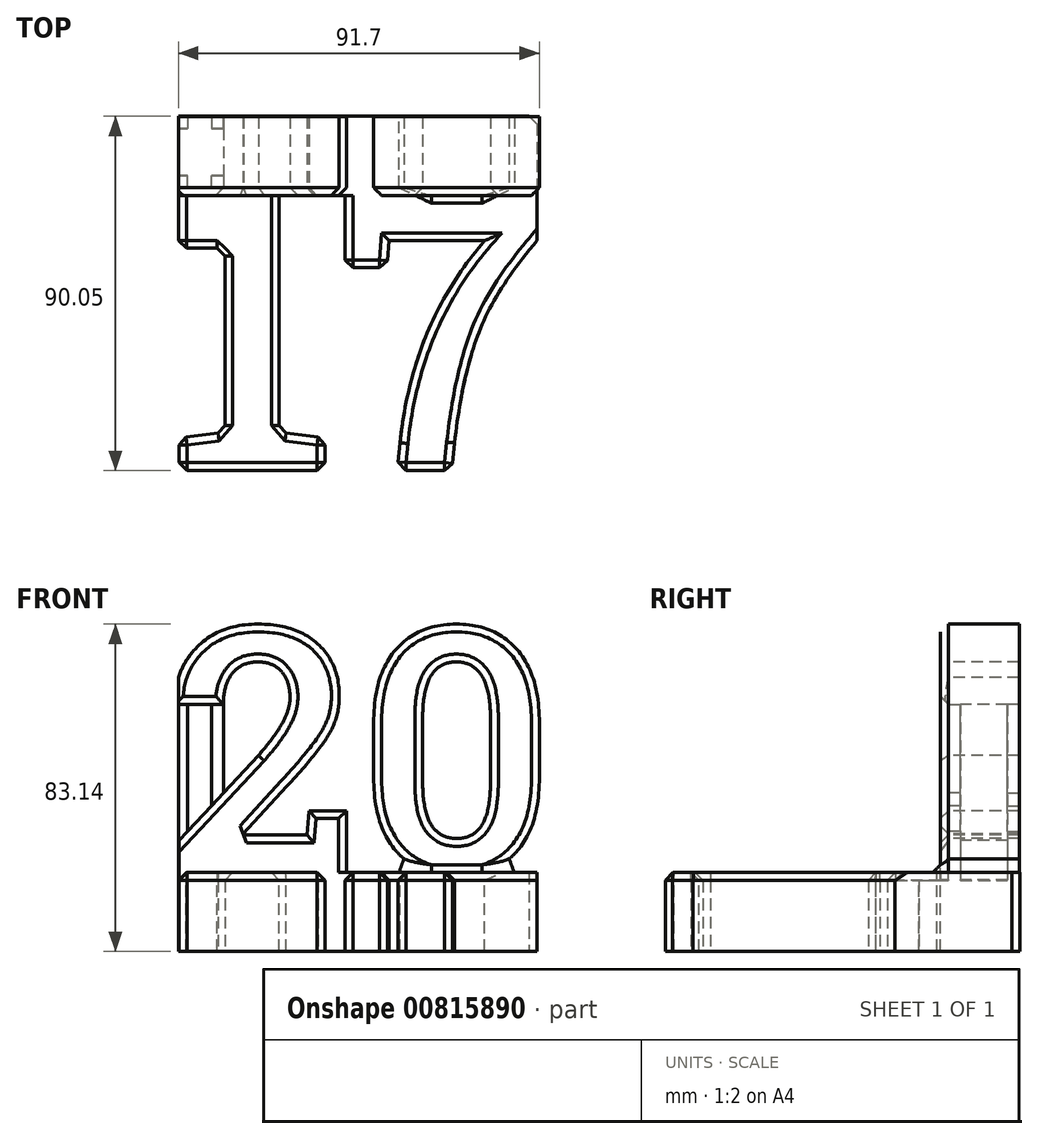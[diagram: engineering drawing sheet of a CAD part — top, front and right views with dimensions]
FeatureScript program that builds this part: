
annotation { "Feature Type Name" : "Feature", "Feature Type Description" : "" }
export const myFeature = defineFeature(function(context is Context, id is Id, definition is map)
    precondition{}
    {
        {
            var Q0;
            Q0=qCreatedBy(makeId("Top.planeOp"),FACE);
            var sketch = newSketch(context, id + "F0", { "sketchPlane" : qUnion([Q0])});
            skText(sketch, "E0", { "text": "17", "fontName": "RobotoSlab-Bold.ttf"});
            const initialGuessF0  = {"E0": [0, -0.06993, 1, 0, 0.06993]};
            skSetInitialGuess(sketch, initialGuessF0);
            skSolve(sketch);
        }
        {
            var Q0;
            Q0=makeQuery(id+"F0.imprint","IMPRINT",FACE,{"disambiguationData":[TD([[makeQuery(id+"F0.imprint","IMPRINT",EDGE,{"derivedFrom":sQuery(id+"F0.wireOp",EDGE,"E0.sketch_text.stroke-0")}),-1.0]])]});
            var Q1;
            Q1=makeQuery(id+"F0.imprint","IMPRINT",FACE,{"disambiguationData":[TD([[makeQuery(id+"F0.imprint","IMPRINT",EDGE,{"derivedFrom":sQuery(id+"F0.wireOp",EDGE,"E0.sketch_text.stroke-10")}),-1.0]])]});
            extrude(context, id + "F1", {"entities" : qUnion([Q0, Q1]), "oppositeDirection" : true, "depth" : 20 * mm, "offsetDistance" : 25 * mm});
        }
        {
            var Q0;
            Q0=qCreatedBy(makeId("Front.planeOp"),FACE);
            var sketch = newSketch(context, id + "F2", { "sketchPlane" : qUnion([Q0])});
            skText(sketch, "E1", { "text": "20", "fontName": "RobotoSlab-Bold.ttf"});
            const initialGuessF2  = {"E1": [0, 0, 1, 0, 0.06303]};
            skSetInitialGuess(sketch, initialGuessF2);
            skSolve(sketch);
        }
        {
            var Q0;
            Q0 = qSketchRegion(id + "F2", true);
            extrude(context, id + "F3", {"entities" : qUnion([Q0]), "oppositeDirection" : true, "depth" : 20 * mm, "offsetDistance" : 25 * mm});
        }
        {
            var Q0;
            Q0=makeQuery(id+"F1.opExtrude","SWEPT_FACE",FACE,{"disambiguationData":[OSD([sQuery(id+"F0.wireOp",EDGE,"E0.sketch_text.stroke-21")])]});
            var sketch = newSketch(context, id + "F4", { "sketchPlane" : qUnion([Q0])});
            skLineSegment(sketch, "E2.bottom", {"start": v(-94.05, -20) * mm, "end": v(0, -20) * mm});
            skLineSegment(sketch, "E2.top", {"start": v(-94.05, 0) * mm, "end": v(0, 0) * mm});
            skLineSegment(sketch, "E2.left", {"start": v(-94.05, -20) * mm, "end": v(-94.05, 0) * mm});
            skLineSegment(sketch, "E2.right", {"start": v(0, -20) * mm, "end": v(0, 0) * mm});
            skSolve(sketch);
        }
        {
            var Q0;
            Q0 = qSketchRegion(id + "F4", true);
            extrude(context, id + "F5", {"entities" : qUnion([Q0]), "operationType" : NewBodyOperationType.ADD, "depth" : 21 * mm, "offsetDistance" : 25 * mm});
        }
        {
            var Q0;
            Q0=makeQuery(id+"F5.opExtrude","CAP_FACE",FACE,{"disambiguationData":[OSD([sQuery(id+"F4.wireOp",EDGE,"E2.bottom"),sQuery(id+"F4.wireOp",EDGE,"E2.top"),sQuery(id+"F4.wireOp",EDGE,"E2.left"),sQuery(id+"F4.wireOp",EDGE,"E2.right")])],"isStart":true});
            var sketch = newSketch(context, id + "F6", { "sketchPlane" : qUnion([Q0])});
            skLineSegment(sketch, "E3.bottom", {"start": v(3, -20) * mm, "end": v(30, -20) * mm});
            skLineSegment(sketch, "E3.top", {"start": v(3, 0) * mm, "end": v(30, 0) * mm});
            skLineSegment(sketch, "E3.left", {"start": v(3, -20) * mm, "end": v(3, 0) * mm});
            skLineSegment(sketch, "E3.right", {"start": v(30, -20) * mm, "end": v(30, 0) * mm});
            skSolve(sketch);
        }
        {
            var Q0;
            Q0 = qSketchRegion(id + "F6", true);
            extrude(context, id + "F7", {"entities" : qUnion([Q0]), "operationType" : NewBodyOperationType.ADD, "depth" : 7 * mm, "offsetDistance" : 25 * mm});
        }
        {
            var Q0;
            Q0=makeQuery(id+"F7.opExtrude","CAP_FACE",FACE,{"disambiguationData":[OSD([sQuery(id+"F6.wireOp",EDGE,"E3.bottom"),sQuery(id+"F6.wireOp",EDGE,"E3.top"),sQuery(id+"F6.wireOp",EDGE,"E3.left"),sQuery(id+"F6.wireOp",EDGE,"E3.right")])],"isStart":false});
            extrude(context, id + "F8", {"entities" : qUnion([Q0]), "operationType" : NewBodyOperationType.REMOVE, "oppositeDirection" : true, "depth" : 7 * mm, "offsetDistance" : 25 * mm});
        }
        {
            var Q0;
            Q0=makeQuery(id+"F7.boolean.opBoolean","MERGE",FACE,{"derivedFrom":[makeQuery(id+"F1.opExtrude","CAP_FACE",FACE,{"disambiguationData":[OSD([sQuery(id+"F0.wireOp",EDGE,"E0.sketch_text.stroke-0"),sQuery(id+"F0.wireOp",EDGE,"E0.sketch_text.stroke-1"),sQuery(id+"F0.wireOp",EDGE,"E0.sketch_text.stroke-2"),sQuery(id+"F0.wireOp",EDGE,"E0.sketch_text.stroke-3"),sQuery(id+"F0.wireOp",EDGE,"E0.sketch_text.stroke-4"),sQuery(id+"F0.wireOp",EDGE,"E0.sketch_text.stroke-5"),sQuery(id+"F0.wireOp",EDGE,"E0.sketch_text.stroke-6"),sQuery(id+"F0.wireOp",EDGE,"E0.sketch_text.stroke-7"),sQuery(id+"F0.wireOp",EDGE,"E0.sketch_text.stroke-8"),sQuery(id+"F0.wireOp",EDGE,"E0.sketch_text.stroke-9")])],"isStart":true}),makeQuery(id+"F5.boolean.opBoolean","MERGE",FACE,{"derivedFrom":[makeQuery(id+"F1.opExtrude","CAP_FACE",FACE,{"disambiguationData":[OSD([sQuery(id+"F0.wireOp",EDGE,"E0.sketch_text.stroke-10"),sQuery(id+"F0.wireOp",EDGE,"E0.sketch_text.stroke-11"),sQuery(id+"F0.wireOp",EDGE,"E0.sketch_text.stroke-12"),sQuery(id+"F0.wireOp",EDGE,"E0.sketch_text.stroke-13"),sQuery(id+"F0.wireOp",EDGE,"E0.sketch_text.stroke-14"),sQuery(id+"F0.wireOp",EDGE,"E0.sketch_text.stroke-15"),sQuery(id+"F0.wireOp",EDGE,"E0.sketch_text.stroke-16"),sQuery(id+"F0.wireOp",EDGE,"E0.sketch_text.stroke-17"),sQuery(id+"F0.wireOp",EDGE,"E0.sketch_text.stroke-18"),sQuery(id+"F0.wireOp",EDGE,"E0.sketch_text.stroke-19"),sQuery(id+"F0.wireOp",EDGE,"E0.sketch_text.stroke-20"),sQuery(id+"F0.wireOp",EDGE,"E0.sketch_text.stroke-21"),sQuery(id+"F0.wireOp",EDGE,"E0.sketch_text.stroke-22")])],"isStart":true}),makeQuery(id+"F5.opExtrude","SWEPT_FACE",FACE,{"disambiguationData":[OSD([sQuery(id+"F4.wireOp",EDGE,"E2.top")])]})]}),makeQuery(id+"F7.opExtrude","SWEPT_FACE",FACE,{"disambiguationData":[OSD([sQuery(id+"F6.wireOp",EDGE,"E3.top")])]})]});
            var sketch = newSketch(context, id + "F9", { "sketchPlane" : qUnion([Q0])});
            skLineSegment(sketch, "E4.bottom", {"start": v(0, 20.12) * mm, "end": v(3, 20.12) * mm});
            skLineSegment(sketch, "E4.top", {"start": v(0, -0.88) * mm, "end": v(3, -0.88) * mm});
            skLineSegment(sketch, "E4.left", {"start": v(0, 20.12) * mm, "end": v(0, -0.88) * mm});
            skLineSegment(sketch, "E4.right", {"start": v(3, 20.12) * mm, "end": v(3, -0.88) * mm});
            skSolve(sketch);
        }
        {
            var Q0;
            Q0 = qSketchRegion(id + "F9", true);
            extrude(context, id + "F10", {"entities" : qUnion([Q0]), "operationType" : NewBodyOperationType.REMOVE, "oppositeDirection" : true, "depth" : 25 * mm, "offsetDistance" : 25 * mm});
        }
        {
            var Q0;
            Q0=makeQuery(id+"F5.boolean.opBoolean","MERGE",EDGE,{"derivedFrom":[makeQuery(id+"F1.opExtrude","CAP_EDGE",EDGE,{"disambiguationData":[OSD([sQuery(id+"F0.wireOp",EDGE,"E0.sketch_text.stroke-22")])],"isStart":true}),makeQuery(id+"F5.opExtrude","SWEPT_EDGE",EDGE,{"disambiguationData":[OSD([sQuery(id+"F4.wireOp",EDGE,"E2.top"),sQuery(id+"F4.wireOp",EDGE,"E2.left")])]})]});
            var Q1;
            Q1=makeQuery(id+"F1.opExtrude","CAP_EDGE",EDGE,{"disambiguationData":[OSD([sQuery(id+"F0.wireOp",EDGE,"E0.sketch_text.stroke-13")])],"isStart":true});
            var Q2;
            Q2=makeQuery(id+"F1.opExtrude","CAP_EDGE",EDGE,{"disambiguationData":[OSD([sQuery(id+"F0.wireOp",EDGE,"E0.sketch_text.stroke-14")])],"isStart":true});
            var Q3;
            Q3=makeQuery(id+"F1.opExtrude","CAP_EDGE",EDGE,{"disambiguationData":[OSD([sQuery(id+"F0.wireOp",EDGE,"E0.sketch_text.stroke-15")])],"isStart":true});
            var Q4;
            Q4=makeQuery(id+"F1.opExtrude","CAP_EDGE",EDGE,{"disambiguationData":[OSD([sQuery(id+"F0.wireOp",EDGE,"E0.sketch_text.stroke-16")])],"isStart":true});
            var Q5;
            Q5=makeQuery(id+"F1.opExtrude","CAP_EDGE",EDGE,{"disambiguationData":[OSD([sQuery(id+"F0.wireOp",EDGE,"E0.sketch_text.stroke-17")])],"isStart":true});
            var Q6;
            Q6=makeQuery(id+"F1.opExtrude","CAP_EDGE",EDGE,{"disambiguationData":[OSD([sQuery(id+"F0.wireOp",EDGE,"E0.sketch_text.stroke-18")])],"isStart":true});
            var Q7;
            Q7=makeQuery(id+"F1.opExtrude","CAP_EDGE",EDGE,{"disambiguationData":[OSD([sQuery(id+"F0.wireOp",EDGE,"E0.sketch_text.stroke-19")])],"isStart":true});
            var Q8;
            Q8=makeQuery(id+"F1.opExtrude","CAP_EDGE",EDGE,{"disambiguationData":[OSD([sQuery(id+"F0.wireOp",EDGE,"E0.sketch_text.stroke-20")])],"isStart":true});
            var Q9;
            Q9=makeQuery(id+"F1.opExtrude","CAP_EDGE",EDGE,{"disambiguationData":[OSD([sQuery(id+"F0.wireOp",EDGE,"E0.sketch_text.stroke-10")])],"isStart":true});
            var Q10;
            Q10=makeQuery(id+"F1.opExtrude","CAP_EDGE",EDGE,{"disambiguationData":[OSD([sQuery(id+"F0.wireOp",EDGE,"E0.sketch_text.stroke-11")])],"isStart":true});
            var Q11;
            Q11=makeQuery(id+"F1.opExtrude","CAP_EDGE",EDGE,{"disambiguationData":[OSD([sQuery(id+"F0.wireOp",EDGE,"E0.sketch_text.stroke-12")])],"isStart":true});
            var Q12;
            {var subQ0=sQuery(id+"F6.wireOp",EDGE,"E3.right");var subQ1=sQuery(id+"F6.wireOp",EDGE,"E3.left");var subQ2=sQuery(id+"F6.wireOp",EDGE,"E3.top");var subQ3=sQuery(id+"F6.wireOp",EDGE,"E3.bottom");var subQ4=sQuery(id+"F0.wireOp",EDGE,"E0.sketch_text.stroke-5");Q12=makeQuery(id+"F8.boolean.opBoolean","MERGE",EDGE,{"derivedFrom":[makeQuery(id+"F1.opExtrude","CAP_EDGE",EDGE,{"disambiguationData":[OSD([subQ4])],"isStart":true}),makeQuery(id+"F8.opExtrude","SWEPT_EDGE",EDGE,{"disambiguationData":[OSD([subQ4,subQ3,subQ2,subQ1,subQ0]),TDD([makeQuery(id+"F7.boolean.opBoolean","INTERSECT",VERTEX,{"disambiguationData":[OD(0.0)],"derivedFrom":[makeQuery(id+"F1.opExtrude","SWEPT_FACE",FACE,{"disambiguationData":[OSD([subQ4])]}),makeQuery(id+"F7.opExtrude","CAP_FACE",FACE,{"disambiguationData":[OSD([subQ3,subQ2,subQ1,subQ0])],"isStart":false})]})])]})]});}
            var Q13;
            Q13=makeQuery(id+"F1.opExtrude","CAP_EDGE",EDGE,{"disambiguationData":[OSD([sQuery(id+"F0.wireOp",EDGE,"E0.sketch_text.stroke-6")])],"isStart":true});
            var Q14;
            Q14=makeQuery(id+"F1.opExtrude","CAP_EDGE",EDGE,{"disambiguationData":[OSD([sQuery(id+"F0.wireOp",EDGE,"E0.sketch_text.stroke-7")])],"isStart":true});
            var Q15;
            Q15=makeQuery(id+"F1.opExtrude","CAP_EDGE",EDGE,{"disambiguationData":[OSD([sQuery(id+"F0.wireOp",EDGE,"E0.sketch_text.stroke-8")])],"isStart":true});
            var Q16;
            Q16=makeQuery(id+"F1.opExtrude","CAP_EDGE",EDGE,{"disambiguationData":[OSD([sQuery(id+"F0.wireOp",EDGE,"E0.sketch_text.stroke-0")])],"isStart":true});
            var Q17;
            Q17=makeQuery(id+"F1.opExtrude","CAP_EDGE",EDGE,{"disambiguationData":[OSD([sQuery(id+"F0.wireOp",EDGE,"E0.sketch_text.stroke-9")])],"isStart":true});
            var Q18;
            Q18=makeQuery(id+"F1.opExtrude","CAP_EDGE",EDGE,{"disambiguationData":[OSD([sQuery(id+"F0.wireOp",EDGE,"E0.sketch_text.stroke-2")])],"isStart":true});
            var Q19;
            Q19=makeQuery(id+"F1.opExtrude","CAP_EDGE",EDGE,{"disambiguationData":[OSD([sQuery(id+"F0.wireOp",EDGE,"E0.sketch_text.stroke-3")])],"isStart":true});
            var Q20;
            Q20=makeQuery(id+"F1.opExtrude","SWEPT_EDGE",EDGE,{"disambiguationData":[OSD([sQuery(id+"F0.wireOp",EDGE,"E0.sketch_text.stroke-7"),sQuery(id+"F0.wireOp",EDGE,"E0.sketch_text.stroke-8")])]});
            var Q21;
            Q21=makeQuery(id+"F1.opExtrude","SWEPT_EDGE",EDGE,{"disambiguationData":[OSD([sQuery(id+"F0.wireOp",EDGE,"E0.sketch_text.stroke-6"),sQuery(id+"F0.wireOp",EDGE,"E0.sketch_text.stroke-7")])]});
            var Q22;
            Q22=makeQuery(id+"F1.opExtrude","SWEPT_EDGE",EDGE,{"disambiguationData":[OSD([sQuery(id+"F0.wireOp",EDGE,"E0.sketch_text.stroke-12"),sQuery(id+"F0.wireOp",EDGE,"E0.sketch_text.stroke-13")])]});
            var Q23;
            Q23=makeQuery(id+"F1.opExtrude","SWEPT_EDGE",EDGE,{"disambiguationData":[OSD([sQuery(id+"F0.wireOp",EDGE,"E0.sketch_text.stroke-13"),sQuery(id+"F0.wireOp",EDGE,"E0.sketch_text.stroke-14")])]});
            var Q24;
            Q24=makeQuery(id+"F5.opExtrude","CAP_EDGE",EDGE,{"disambiguationData":[OSD([sQuery(id+"F4.wireOp",EDGE,"E2.left")])],"isStart":false});
            var Q25;
            Q25=makeQuery(id+"F1.opExtrude","SWEPT_EDGE",EDGE,{"disambiguationData":[OSD([sQuery(id+"F0.wireOp",EDGE,"E0.sketch_text.stroke-8"),sQuery(id+"F0.wireOp",EDGE,"E0.sketch_text.stroke-9")])]});
            var Q26;
            Q26=makeQuery(id+"F1.opExtrude","SWEPT_EDGE",EDGE,{"disambiguationData":[OSD([sQuery(id+"F0.wireOp",EDGE,"E0.sketch_text.stroke-5"),sQuery(id+"F0.wireOp",EDGE,"E0.sketch_text.stroke-6")])]});
            var Q27;
            Q27=makeQuery(id+"F1.opExtrude","SWEPT_EDGE",EDGE,{"disambiguationData":[OSD([sQuery(id+"F0.wireOp",EDGE,"E0.sketch_text.stroke-0"),sQuery(id+"F0.wireOp",EDGE,"E0.sketch_text.stroke-1")])]});
            var Q28;
            Q28=makeQuery(id+"F1.opExtrude","SWEPT_EDGE",EDGE,{"disambiguationData":[OSD([sQuery(id+"F0.wireOp",EDGE,"E0.sketch_text.stroke-0"),sQuery(id+"F0.wireOp",EDGE,"E0.sketch_text.stroke-9")])]});
            var Q29;
            Q29=makeQuery(id+"F1.opExtrude","SWEPT_EDGE",EDGE,{"disambiguationData":[OSD([sQuery(id+"F0.wireOp",EDGE,"E0.sketch_text.stroke-2"),sQuery(id+"F0.wireOp",EDGE,"E0.sketch_text.stroke-3")])]});
            var Q30;
            Q30=makeQuery(id+"F1.opExtrude","SWEPT_EDGE",EDGE,{"disambiguationData":[OSD([sQuery(id+"F0.wireOp",EDGE,"E0.sketch_text.stroke-1"),sQuery(id+"F0.wireOp",EDGE,"E0.sketch_text.stroke-2")])]});
            var Q31;
            Q31=makeQuery(id+"F1.opExtrude","SWEPT_EDGE",EDGE,{"disambiguationData":[OSD([sQuery(id+"F0.wireOp",EDGE,"E0.sketch_text.stroke-19"),sQuery(id+"F0.wireOp",EDGE,"E0.sketch_text.stroke-20")])]});
            var Q32;
            Q32=makeQuery(id+"F1.opExtrude","SWEPT_EDGE",EDGE,{"disambiguationData":[OSD([sQuery(id+"F0.wireOp",EDGE,"E0.sketch_text.stroke-18"),sQuery(id+"F0.wireOp",EDGE,"E0.sketch_text.stroke-19")])]});
            var Q33;
            Q33=makeQuery(id+"F3.opExtrude","CAP_FACE",FACE,{"disambiguationData":[OSD([sQuery(id+"F2.wireOp",EDGE,"E1.sketch_text.stroke-23"),sQuery(id+"F2.wireOp",EDGE,"E1.sketch_text.stroke-24"),sQuery(id+"F2.wireOp",EDGE,"E1.sketch_text.stroke-25"),sQuery(id+"F2.wireOp",EDGE,"E1.sketch_text.stroke-26"),sQuery(id+"F2.wireOp",EDGE,"E1.sketch_text.stroke-27"),sQuery(id+"F2.wireOp",EDGE,"E1.sketch_text.stroke-28"),sQuery(id+"F2.wireOp",EDGE,"E1.sketch_text.stroke-29"),sQuery(id+"F2.wireOp",EDGE,"E1.sketch_text.stroke-30"),sQuery(id+"F2.wireOp",EDGE,"E1.sketch_text.stroke-31"),sQuery(id+"F2.wireOp",EDGE,"E1.sketch_text.stroke-32"),sQuery(id+"F2.wireOp",EDGE,"E1.sketch_text.stroke-33"),sQuery(id+"F2.wireOp",EDGE,"E1.sketch_text.stroke-34"),sQuery(id+"F2.wireOp",EDGE,"E1.sketch_text.stroke-35"),sQuery(id+"F2.wireOp",EDGE,"E1.sketch_text.stroke-36"),sQuery(id+"F2.wireOp",EDGE,"E1.sketch_text.stroke-37"),sQuery(id+"F2.wireOp",EDGE,"E1.sketch_text.stroke-38"),sQuery(id+"F2.wireOp",EDGE,"E1.sketch_text.stroke-39"),sQuery(id+"F2.wireOp",EDGE,"E1.sketch_text.stroke-40"),sQuery(id+"F2.wireOp",EDGE,"E1.sketch_text.stroke-41"),sQuery(id+"F2.wireOp",EDGE,"E1.sketch_text.stroke-42")])],"isStart":true});
            var Q34;
            Q34=makeQuery(id+"F3.opExtrude","CAP_EDGE",EDGE,{"disambiguationData":[OSD([sQuery(id+"F2.wireOp",EDGE,"E1.sketch_text.stroke-8")])],"isStart":true});
            var Q35;
            Q35=makeQuery(id+"F3.opExtrude","CAP_EDGE",EDGE,{"disambiguationData":[OSD([sQuery(id+"F2.wireOp",EDGE,"E1.sketch_text.stroke-10")])],"isStart":true});
            var Q36;
            Q36=makeQuery(id+"F3.opExtrude","CAP_EDGE",EDGE,{"disambiguationData":[OSD([sQuery(id+"F2.wireOp",EDGE,"E1.sketch_text.stroke-18")])],"isStart":true});
            var Q37;
            Q37=makeQuery(id+"F3.opExtrude","CAP_EDGE",EDGE,{"disambiguationData":[OSD([sQuery(id+"F2.wireOp",EDGE,"E1.sketch_text.stroke-19")])],"isStart":true});
            var Q38;
            Q38=makeQuery(id+"F3.opExtrude","CAP_EDGE",EDGE,{"disambiguationData":[OSD([sQuery(id+"F2.wireOp",EDGE,"E1.sketch_text.stroke-20")])],"isStart":true});
            var Q39;
            Q39=makeQuery(id+"F3.opExtrude","CAP_EDGE",EDGE,{"disambiguationData":[OSD([sQuery(id+"F2.wireOp",EDGE,"E1.sketch_text.stroke-21")])],"isStart":true});
            var Q40;
            Q40=makeQuery(id+"F3.opExtrude","CAP_EDGE",EDGE,{"disambiguationData":[OSD([sQuery(id+"F2.wireOp",EDGE,"E1.sketch_text.stroke-7")])],"isStart":true});
            var Q41;
            Q41=makeQuery(id+"F3.opExtrude","CAP_EDGE",EDGE,{"disambiguationData":[OSD([sQuery(id+"F2.wireOp",EDGE,"E1.sketch_text.stroke-6")])],"isStart":true});
            chamfer(context, id + "F11", {"entities" : qUnion([Q0, Q1, Q2, Q3, Q4, Q5, Q6, Q7, Q8, Q9, Q10, Q11, Q12, Q13, Q14, Q15, Q16, Q17, Q18, Q19, Q20, Q21, Q22, Q23, Q24, Q25, Q26, Q27, Q28, Q29, Q30, Q31, Q32, Q33, Q34, Q35, Q36, Q37, Q38, Q39, Q40, Q41]), "width" : 2 * mm, "tangentPropagation" : true});
        }
        {
            var Q0;
            Q0=makeQuery(id+"F7.boolean.opBoolean","MERGE",FACE,{"derivedFrom":[makeQuery(id+"F1.opExtrude","CAP_FACE",FACE,{"disambiguationData":[OSD([sQuery(id+"F0.wireOp",EDGE,"E0.sketch_text.stroke-0"),sQuery(id+"F0.wireOp",EDGE,"E0.sketch_text.stroke-1"),sQuery(id+"F0.wireOp",EDGE,"E0.sketch_text.stroke-2"),sQuery(id+"F0.wireOp",EDGE,"E0.sketch_text.stroke-3"),sQuery(id+"F0.wireOp",EDGE,"E0.sketch_text.stroke-4"),sQuery(id+"F0.wireOp",EDGE,"E0.sketch_text.stroke-5"),sQuery(id+"F0.wireOp",EDGE,"E0.sketch_text.stroke-6"),sQuery(id+"F0.wireOp",EDGE,"E0.sketch_text.stroke-7"),sQuery(id+"F0.wireOp",EDGE,"E0.sketch_text.stroke-8"),sQuery(id+"F0.wireOp",EDGE,"E0.sketch_text.stroke-9")])],"isStart":true}),makeQuery(id+"F5.boolean.opBoolean","MERGE",FACE,{"derivedFrom":[makeQuery(id+"F1.opExtrude","CAP_FACE",FACE,{"disambiguationData":[OSD([sQuery(id+"F0.wireOp",EDGE,"E0.sketch_text.stroke-10"),sQuery(id+"F0.wireOp",EDGE,"E0.sketch_text.stroke-11"),sQuery(id+"F0.wireOp",EDGE,"E0.sketch_text.stroke-12"),sQuery(id+"F0.wireOp",EDGE,"E0.sketch_text.stroke-13"),sQuery(id+"F0.wireOp",EDGE,"E0.sketch_text.stroke-14"),sQuery(id+"F0.wireOp",EDGE,"E0.sketch_text.stroke-15"),sQuery(id+"F0.wireOp",EDGE,"E0.sketch_text.stroke-16"),sQuery(id+"F0.wireOp",EDGE,"E0.sketch_text.stroke-17"),sQuery(id+"F0.wireOp",EDGE,"E0.sketch_text.stroke-18"),sQuery(id+"F0.wireOp",EDGE,"E0.sketch_text.stroke-19"),sQuery(id+"F0.wireOp",EDGE,"E0.sketch_text.stroke-20"),sQuery(id+"F0.wireOp",EDGE,"E0.sketch_text.stroke-21"),sQuery(id+"F0.wireOp",EDGE,"E0.sketch_text.stroke-22")])],"isStart":true}),makeQuery(id+"F5.opExtrude","SWEPT_FACE",FACE,{"disambiguationData":[OSD([sQuery(id+"F4.wireOp",EDGE,"E2.top")])]})]}),makeQuery(id+"F7.opExtrude","SWEPT_FACE",FACE,{"disambiguationData":[OSD([sQuery(id+"F6.wireOp",EDGE,"E3.top")])]})]});
            var sketch = newSketch(context, id + "F12", { "sketchPlane" : qUnion([Q0])});
            skLineSegment(sketch, "E5.bottom", {"start": v(26.55, -0.88) * mm, "end": v(47.24, -0.88) * mm});
            skLineSegment(sketch, "E5.top", {"start": v(26.55, 0) * mm, "end": v(47.24, 0) * mm});
            skLineSegment(sketch, "E5.left", {"start": v(26.55, -0.88) * mm, "end": v(26.55, 0) * mm});
            skLineSegment(sketch, "E5.right", {"start": v(47.24, -0.88) * mm, "end": v(47.24, 0) * mm});
            skSolve(sketch);
        }
        {
            var Q0;
            Q0 = qSketchRegion(id + "F12", true);
            extrude(context, id + "F13", {"entities" : qUnion([Q0]), "operationType" : NewBodyOperationType.REMOVE, "oppositeDirection" : true, "depth" : 25 * mm, "offsetDistance" : 25 * mm});
        }
        {
            var Q0;
            {var subQ5=sQuery(id+"F0.wireOp",EDGE,"E0.sketch_text.stroke-5");Q0=makeQuery(id+"F13.boolean.opBoolean","COPY",FACE,{"disambiguationData":[TD([makeQuery(id+"F1.opExtrude","SWEPT_FACE",FACE,{"disambiguationData":[OSD([subQ5])]})])],"derivedFrom":makeQuery(id+"F13.opExtrude","SWEPT_FACE",FACE,{"disambiguationData":[OSD([sQuery(id+"F12.wireOp",EDGE,"E5.bottom")])]})});}
            var Q1;
            {var subQ0=sQuery(id+"F0.wireOp",EDGE,"E0.sketch_text.stroke-20");Q1=makeQuery(id+"F13.boolean.opBoolean","COPY",FACE,{"disambiguationData":[TD([makeQuery(id+"F1.opExtrude","SWEPT_FACE",FACE,{"disambiguationData":[OSD([subQ0])]})])],"derivedFrom":makeQuery(id+"F13.opExtrude","SWEPT_FACE",FACE,{"disambiguationData":[OSD([sQuery(id+"F12.wireOp",EDGE,"E5.bottom")])]})});}
            extrude(context, id + "F14", {"entities" : qUnion([Q0, Q1]), "operationType" : NewBodyOperationType.ADD, "depth" : 15 * mm, "offsetDistance" : 25 * mm});
        }
        {
            var Q0;
            Q0=makeQuery(id+"F3.opExtrude","SWEPT_FACE",FACE,{"disambiguationData":[OSD([sQuery(id+"F2.wireOp",EDGE,"E1.sketch_text.stroke-8")])]});
            var sketch = newSketch(context, id + "F15", { "sketchPlane" : qUnion([Q0])});
            skLineSegment(sketch, "E6.bottom", {"start": v(2.23, -2) * mm, "end": v(5.23, -2) * mm});
            skLineSegment(sketch, "E6.top", {"start": v(2.23, -5) * mm, "end": v(5.23, -5) * mm});
            skLineSegment(sketch, "E6.left", {"start": v(2.23, -2) * mm, "end": v(2.23, -5) * mm});
            skLineSegment(sketch, "E6.right", {"start": v(5.23, -2) * mm, "end": v(5.23, -5) * mm});
            skPoint(sketch, "E7.oppositeSnap0", {"position": v(5.23, -3.5) * mm});
            skLineSegment(sketch, "E7.bottom", {"start": v(2.23, -20) * mm, "end": v(5.23, -20) * mm});
            skLineSegment(sketch, "E7.top", {"start": v(2.23, -17) * mm, "end": v(5.23, -17) * mm});
            skLineSegment(sketch, "E7.left", {"start": v(2.23, -20) * mm, "end": v(2.23, -17) * mm});
            skLineSegment(sketch, "E7.right", {"start": v(5.23, -20) * mm, "end": v(5.23, -17) * mm});
            skLineSegment(sketch, "E8.bottom", {"start": v(14.36, -20) * mm, "end": v(11.36, -20) * mm});
            skLineSegment(sketch, "E8.top", {"start": v(14.36, -17) * mm, "end": v(11.36, -17) * mm});
            skLineSegment(sketch, "E8.left", {"start": v(14.36, -20) * mm, "end": v(14.36, -17) * mm});
            skLineSegment(sketch, "E8.right", {"start": v(11.36, -20) * mm, "end": v(11.36, -17) * mm});
            skLineSegment(sketch, "E9.bottom", {"start": v(14.36, -2) * mm, "end": v(11.36, -2) * mm});
            skLineSegment(sketch, "E9.top", {"start": v(14.36, -5) * mm, "end": v(11.36, -5) * mm});
            skLineSegment(sketch, "E9.left", {"start": v(14.36, -2) * mm, "end": v(14.36, -5) * mm});
            skLineSegment(sketch, "E9.right", {"start": v(11.36, -2) * mm, "end": v(11.36, -5) * mm});
            skSolve(sketch);
        }
        {
            var Q0;
            Q0 = qSketchRegion(id + "F15", true);
            extrude(context, id + "F16", {"entities" : qUnion([Q0]), "operationType" : NewBodyOperationType.ADD, "depth" : 58.4 * mm, "offsetDistance" : 25 * mm});
        }
        {
            var Q0;
            {var subQ0=sQuery(id+"F12.wireOp",EDGE,"E5.bottom");var subQ1=makeQuery(id+"F13.opExtrude","SWEPT_FACE",FACE,{"disambiguationData":[OSD([subQ0])]});var subQ2=sQuery(id+"F6.wireOp",EDGE,"E3.bottom");var subQ3=sQuery(id+"F4.wireOp",EDGE,"E2.bottom");var subQ4=sQuery(id+"F0.wireOp",EDGE,"E0.sketch_text.stroke-22");var subQ5=sQuery(id+"F0.wireOp",EDGE,"E0.sketch_text.stroke-21");var subQ6=sQuery(id+"F0.wireOp",EDGE,"E0.sketch_text.stroke-20");var subQ7=sQuery(id+"F0.wireOp",EDGE,"E0.sketch_text.stroke-19");var subQ8=sQuery(id+"F0.wireOp",EDGE,"E0.sketch_text.stroke-18");var subQ9=sQuery(id+"F0.wireOp",EDGE,"E0.sketch_text.stroke-17");var subQ10=sQuery(id+"F0.wireOp",EDGE,"E0.sketch_text.stroke-16");var subQ11=sQuery(id+"F0.wireOp",EDGE,"E0.sketch_text.stroke-15");var subQ12=sQuery(id+"F0.wireOp",EDGE,"E0.sketch_text.stroke-14");var subQ13=sQuery(id+"F0.wireOp",EDGE,"E0.sketch_text.stroke-13");var subQ14=sQuery(id+"F0.wireOp",EDGE,"E0.sketch_text.stroke-12");var subQ15=sQuery(id+"F0.wireOp",EDGE,"E0.sketch_text.stroke-11");var subQ16=sQuery(id+"F0.wireOp",EDGE,"E0.sketch_text.stroke-10");var subQ17=sQuery(id+"F0.wireOp",EDGE,"E0.sketch_text.stroke-9");var subQ18=sQuery(id+"F0.wireOp",EDGE,"E0.sketch_text.stroke-8");var subQ19=sQuery(id+"F0.wireOp",EDGE,"E0.sketch_text.stroke-7");var subQ20=sQuery(id+"F0.wireOp",EDGE,"E0.sketch_text.stroke-6");var subQ21=sQuery(id+"F0.wireOp",EDGE,"E0.sketch_text.stroke-5");var subQ22=sQuery(id+"F0.wireOp",EDGE,"E0.sketch_text.stroke-4");var subQ23=sQuery(id+"F0.wireOp",EDGE,"E0.sketch_text.stroke-3");var subQ24=sQuery(id+"F0.wireOp",EDGE,"E0.sketch_text.stroke-2");var subQ25=sQuery(id+"F0.wireOp",EDGE,"E0.sketch_text.stroke-1");var subQ26=sQuery(id+"F0.wireOp",EDGE,"E0.sketch_text.stroke-0");var subQ27=makeQuery(id+"F7.boolean.opBoolean","MERGE",FACE,{"derivedFrom":[makeQuery(id+"F1.opExtrude","CAP_FACE",FACE,{"disambiguationData":[OSD([subQ26,subQ25,subQ24,subQ23,subQ22,subQ21,subQ20,subQ19,subQ18,subQ17])],"isStart":false}),makeQuery(id+"F5.boolean.opBoolean","MERGE",FACE,{"derivedFrom":[makeQuery(id+"F1.opExtrude","CAP_FACE",FACE,{"disambiguationData":[OSD([subQ16,subQ15,subQ14,subQ13,subQ12,subQ11,subQ10,subQ9,subQ8,subQ7,subQ6,subQ5,subQ4])],"isStart":false}),makeQuery(id+"F5.opExtrude","SWEPT_FACE",FACE,{"disambiguationData":[OSD([subQ3])]})]}),makeQuery(id+"F7.opExtrude","SWEPT_FACE",FACE,{"disambiguationData":[OSD([subQ2])]})]});Q0=makeQuery(id+"F14.boolean.opBoolean","MERGE",FACE,{"derivedFrom":[subQ27,makeQuery(id+"F14.opExtrude","SWEPT_FACE",FACE,{"disambiguationData":[OSD([subQ26,subQ25,subQ24,subQ23,subQ22,subQ21,subQ20,subQ19,subQ18,subQ17,subQ16,subQ15,subQ14,subQ13,subQ12,subQ11,subQ10,subQ9,subQ8,subQ7,subQ6,subQ5,subQ4,subQ3,subQ2,subQ0]),TDD([makeQuery(id+"F13.boolean.opBoolean","INTERSECT",EDGE,{"disambiguationData":[OD(0.0)],"derivedFrom":[subQ27,subQ1]})])]}),makeQuery(id+"F14.opExtrude","SWEPT_FACE",FACE,{"disambiguationData":[OSD([subQ26,subQ25,subQ24,subQ23,subQ22,subQ21,subQ20,subQ19,subQ18,subQ17,subQ16,subQ15,subQ14,subQ13,subQ12,subQ11,subQ10,subQ9,subQ8,subQ7,subQ6,subQ5,subQ4,subQ3,subQ2,subQ0]),TDD([makeQuery(id+"F13.boolean.opBoolean","INTERSECT",EDGE,{"disambiguationData":[OD(1.0)],"derivedFrom":[subQ27,subQ1]})])]})]});}
            var sketch = newSketch(context, id + "F17", { "sketchPlane" : qUnion([Q0])});
            skLineSegment(sketch, "E10.bottom", {"start": v(3, -20.12) * mm, "end": v(-14.35, -20.12) * mm});
            skLineSegment(sketch, "E10.top", {"start": v(3, 0.47) * mm, "end": v(-14.35, 0.47) * mm});
            skLineSegment(sketch, "E10.left", {"start": v(3, -20.12) * mm, "end": v(3, 0.47) * mm});
            skLineSegment(sketch, "E10.right", {"start": v(-14.35, -20.12) * mm, "end": v(-14.35, 0.47) * mm});
            skSolve(sketch);
        }
        {
            var Q0;
            Q0 = qSketchRegion(id + "F17", true);
            extrude(context, id + "F18", {"entities" : qUnion([Q0]), "operationType" : NewBodyOperationType.REMOVE, "oppositeDirection" : true, "depth" : 94.3 * mm, "offsetDistance" : 25 * mm});
        }
    });
